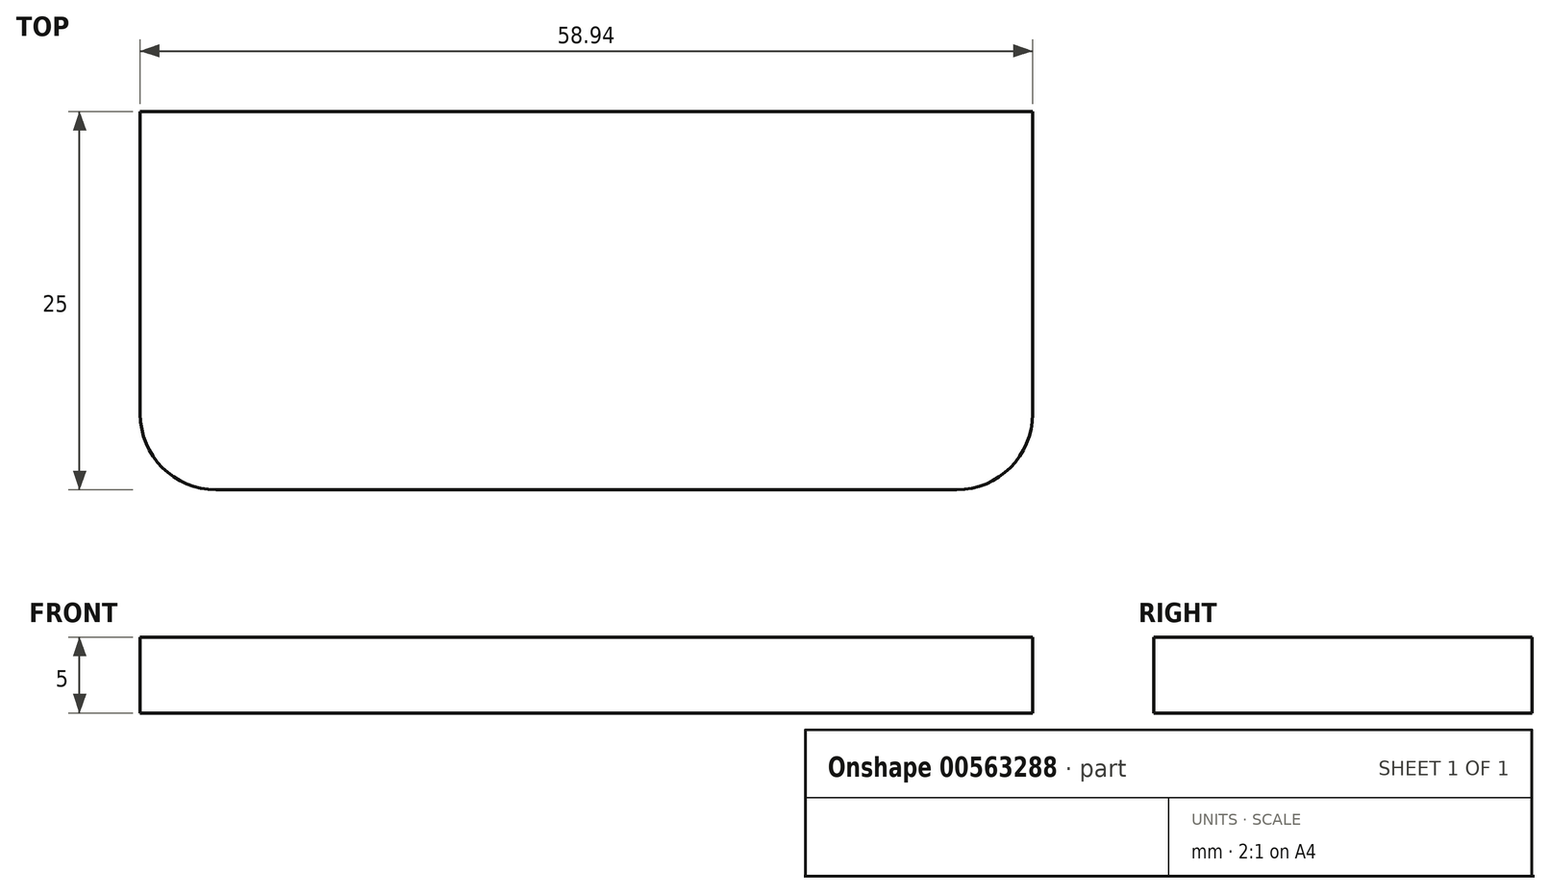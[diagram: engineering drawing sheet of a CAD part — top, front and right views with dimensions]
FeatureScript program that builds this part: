
annotation { "Feature Type Name" : "Feature", "Feature Type Description" : "" }
export const myFeature = defineFeature(function(context is Context, id is Id, definition is map)
    precondition{}
    {
        {
            var Q0;
            Q0=qCreatedBy(makeId("Top.planeOp"),FACE);
            var sketch = newSketch(context, id + "F0", { "sketchPlane" : qUnion([Q0])});
            skLineSegment(sketch, "E0.bottom", {"start": v(0.12, -2.62) * mm, "end": v(59.06, -2.62) * mm});
            skLineSegment(sketch, "E0.top", {"start": v(5.12, -27.62) * mm, "end": v(54.06, -27.62) * mm});
            skLineSegment(sketch, "E0.left", {"start": v(0.12, -2.62) * mm, "end": v(0.12, -22.62) * mm});
            skLineSegment(sketch, "E0.right", {"start": v(59.06, -2.62) * mm, "end": v(59.06, -22.62) * mm});
            skPoint(sketch, "E1.visualSharp", {"position": v(0.12, -27.62) * mm});
            skArc(sketch, "E1.filletArc", {"start": v(0.12, -22.62) * mm, "mid": v(1.59, -26.15) * mm, "end": v(5.12, -27.62) * mm});
            skPoint(sketch, "E2.visualSharp", {"position": v(59.06, -27.62) * mm});
            skArc(sketch, "E2.filletArc", {"start": v(54.06, -27.62) * mm, "mid": v(57.6, -26.15) * mm, "end": v(59.06, -22.62) * mm});
            skSolve(sketch);
        }
        {
            var Q0;
            Q0 = qSketchRegion(id + "F0", true);
            extrude(context, id + "F1", {"entities" : qUnion([Q0]), "depth" : 5 * mm, "offsetDistance" : 25 * mm});
        }
    });
